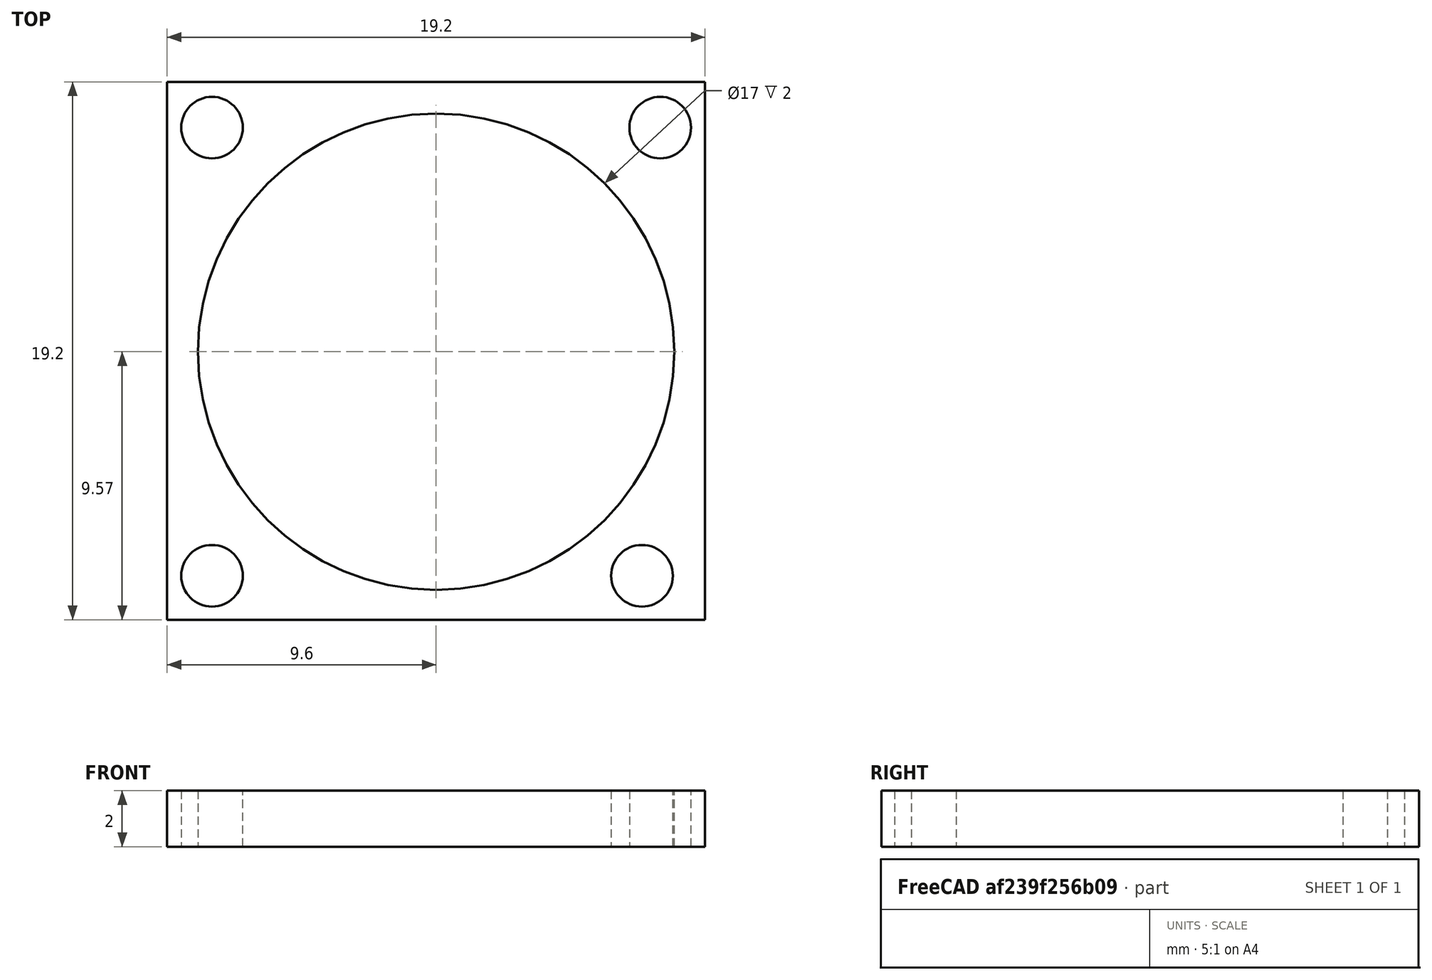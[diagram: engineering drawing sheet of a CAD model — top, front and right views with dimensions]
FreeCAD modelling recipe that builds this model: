
FCSTD DOCUMENT  (FreeCAD 0.18.4R)
Label: ring_for_nema8
License: All rights reserved
LicenseURL: http://en.wikipedia.org/wiki/All_rights_reserved
objects: Sketcher::SketchObject×1, PartDesign::Pad×1, PartDesign::Body×1
note: 4 computed .brp shape members not serialized (recipe doc carries the construction recipe); baked Part::Feature solids carry a one-line shape summary decoded from their .brp

FEATURE [Sketcher::SketchObject] Sketch
  MapMode = 5
  Support = -> [XY_Plane]
  sketch-geometry (9):
    g0: LineSegment StartX=-9.6 StartY=9.62929 StartZ=0 EndX=9.6 EndY=9.62929 EndZ=0
    g1: LineSegment StartX=9.6 StartY=9.62929 StartZ=0 EndX=9.6 EndY=-9.57071 EndZ=0
    g2: LineSegment StartX=9.6 StartY=-9.57071 StartZ=0 EndX=-9.6 EndY=-9.57071 EndZ=0
    g3: LineSegment StartX=-9.6 StartY=-9.57071 StartZ=0 EndX=-9.6 EndY=9.62929 EndZ=0
    g4: Circle CenterX=0 CenterY=0 CenterZ=0 NormalX=0 NormalY=0 NormalZ=1 AngleXU=0 Radius=8.5
    g5: Circle CenterX=-8 CenterY=8 CenterZ=0 NormalX=0 NormalY=0 NormalZ=1 AngleXU=0 Radius=1.1
    g6: Circle CenterX=8 CenterY=8 CenterZ=0 NormalX=0 NormalY=0 NormalZ=1 AngleXU=0 Radius=1.1
    g7: Circle CenterX=7.3481 CenterY=-8 CenterZ=0 NormalX=0 NormalY=0 NormalZ=1 AngleXU=0 Radius=1.1
    g8: Circle CenterX=-8 CenterY=-8 CenterZ=0 NormalX=0 NormalY=0 NormalZ=1 AngleXU=0 Radius=1.1
  constraints (21):
    c: Coincident(g0,g1)
    c: Coincident(g1,g2)
    c: Coincident(g2,g3)
    c: Coincident(g3,g0)
    c: Horizontal(g2)
    c: Vertical(g1)
    c: Symmetric(g0,g0,g-2)
    c: DistanceX(g0,g0) = 19.2
    c: Coincident(g4,g-1)
    c: Radius(g4) = 8.5
    c: Horizontal(g8,g7)
    c: Distance(g5,g6) = 16
    c: Symmetric(g5,g8,g-1)
    c: Symmetric(g5,g6,g-2)
    c: Radius(g7) = 1.1
    c: Radius(g6) = 1.1
    c: Radius(g5) = 1.1
    c: Radius(g8) = 1.1
    c: DistanceX(g2,g2) = 19.2
    c: Distance(g8,g5) = 16
    c: DistanceY(g3,g3) = 19.2
FEATURE [PartDesign::Pad] Pad
  Length = 2
  Length2 = 100
  Profile = -> Sketch
  Type = 0
FEATURE [PartDesign::Body] Body
  Group = -> [Sketch,Pad]
  Origin = -> Origin
  Tip = -> Pad
